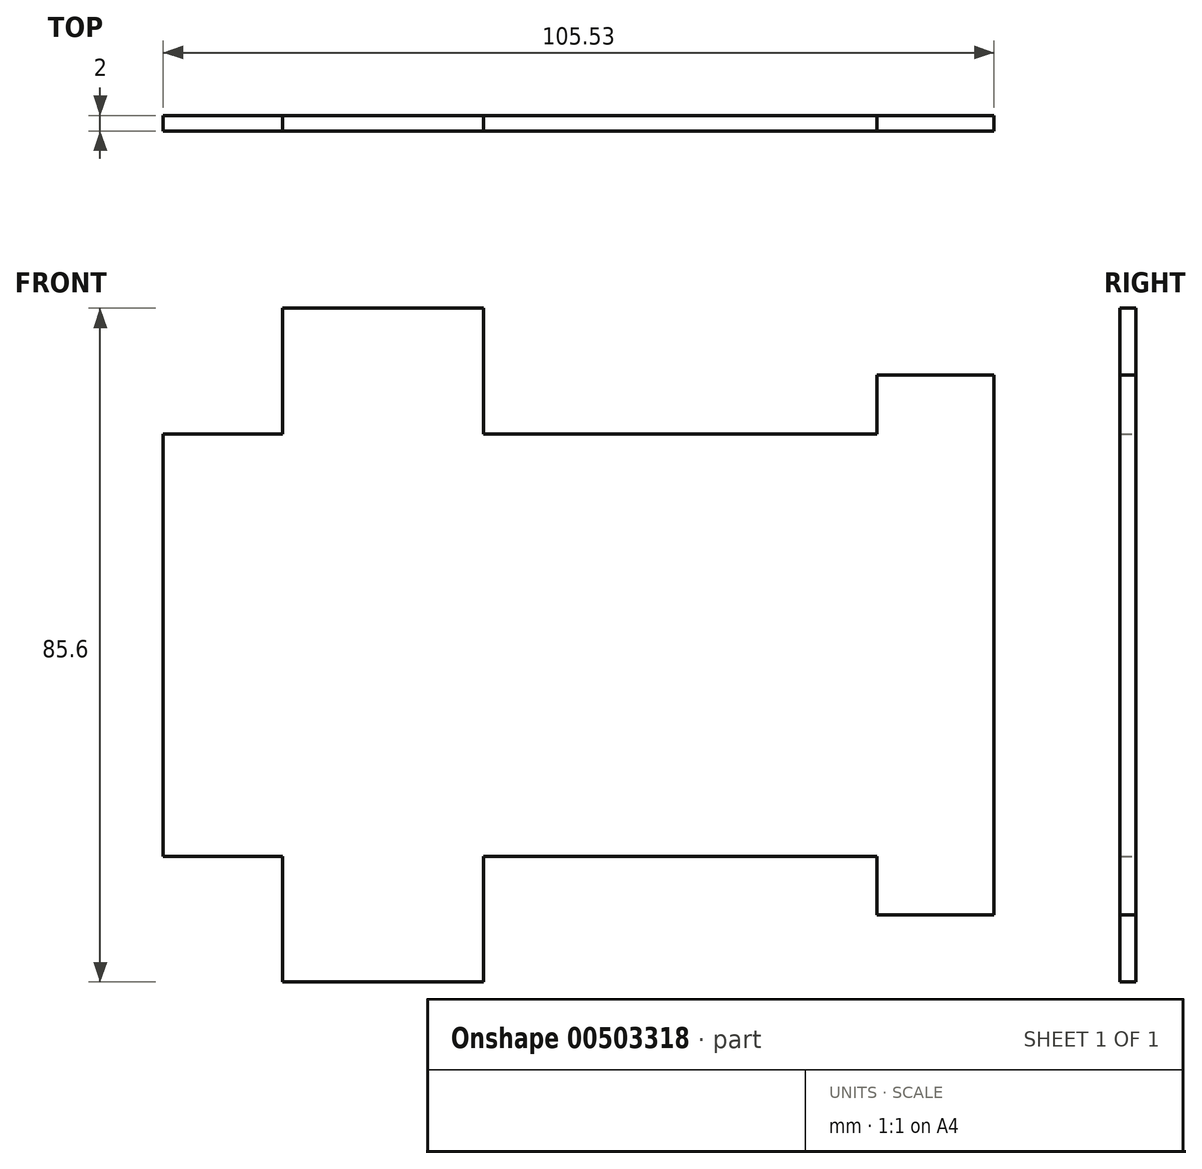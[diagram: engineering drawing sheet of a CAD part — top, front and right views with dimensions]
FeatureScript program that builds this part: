
annotation { "Feature Type Name" : "Feature", "Feature Type Description" : "" }
export const myFeature = defineFeature(function(context is Context, id is Id, definition is map)
    precondition{}
    {
        {
            var Q0;
            Q0=qCreatedBy(makeId("Front.planeOp"),FACE);
            var sketch = newSketch(context, id + "F0", { "sketchPlane" : qUnion([Q0])});
            skLineSegment(sketch, "E0", {"start": v(0, 0) * mm, "end": v(105.53, 0) * mm});
            skLineSegment(sketch, "E1", {"start": v(105.53, 0) * mm, "end": v(105.53, 34.3) * mm});
            skLineSegment(sketch, "E2", {"start": v(105.53, 34.3) * mm, "end": v(90.64, 34.3) * mm});
            skLineSegment(sketch, "E3", {"start": v(90.64, 34.3) * mm, "end": v(90.64, 26.85) * mm});
            skLineSegment(sketch, "E4", {"start": v(90.64, 26.85) * mm, "end": v(40.67, 26.85) * mm});
            skLineSegment(sketch, "E5", {"start": v(40.67, 26.85) * mm, "end": v(40.67, 42.8) * mm});
            skLineSegment(sketch, "E6", {"start": v(40.67, 42.8) * mm, "end": v(15.15, 42.8) * mm});
            skLineSegment(sketch, "E7", {"start": v(15.15, 42.8) * mm, "end": v(15.15, 26.85) * mm});
            skLineSegment(sketch, "E8", {"start": v(15.15, 26.85) * mm, "end": v(0, 26.85) * mm});
            skLineSegment(sketch, "E9", {"start": v(0, 26.85) * mm, "end": v(0, 0) * mm});
            skSolve(sketch);
        }
        {
            var Q0;
            Q0 = qSketchRegion(id + "F0", true);
            extrude(context, id + "F1", {"entities" : qUnion([Q0]), "depth" : 2 * mm});
        }
        {
            var Q0;
            Q0=makeQuery(id+"F1.opExtrude","SWEPT_BODY",BODY,{"disambiguationData":[OSD([sQuery(id+"F0.wireOp",EDGE,"E0"),sQuery(id+"F0.wireOp",EDGE,"E1"),sQuery(id+"F0.wireOp",EDGE,"E2"),sQuery(id+"F0.wireOp",EDGE,"E3"),sQuery(id+"F0.wireOp",EDGE,"E4"),sQuery(id+"F0.wireOp",EDGE,"E5"),sQuery(id+"F0.wireOp",EDGE,"E6"),sQuery(id+"F0.wireOp",EDGE,"E7"),sQuery(id+"F0.wireOp",EDGE,"E8"),sQuery(id+"F0.wireOp",EDGE,"E9")])]});
            var Q1;
            Q1=qCreatedBy(makeId("Top.planeOp"),FACE);
            mirror(context, id + "F2", {"operationType" : NewBodyOperationType.ADD, "entities" : qUnion([Q0]), "mirrorPlane" : qUnion([Q1])});
        }
    });
